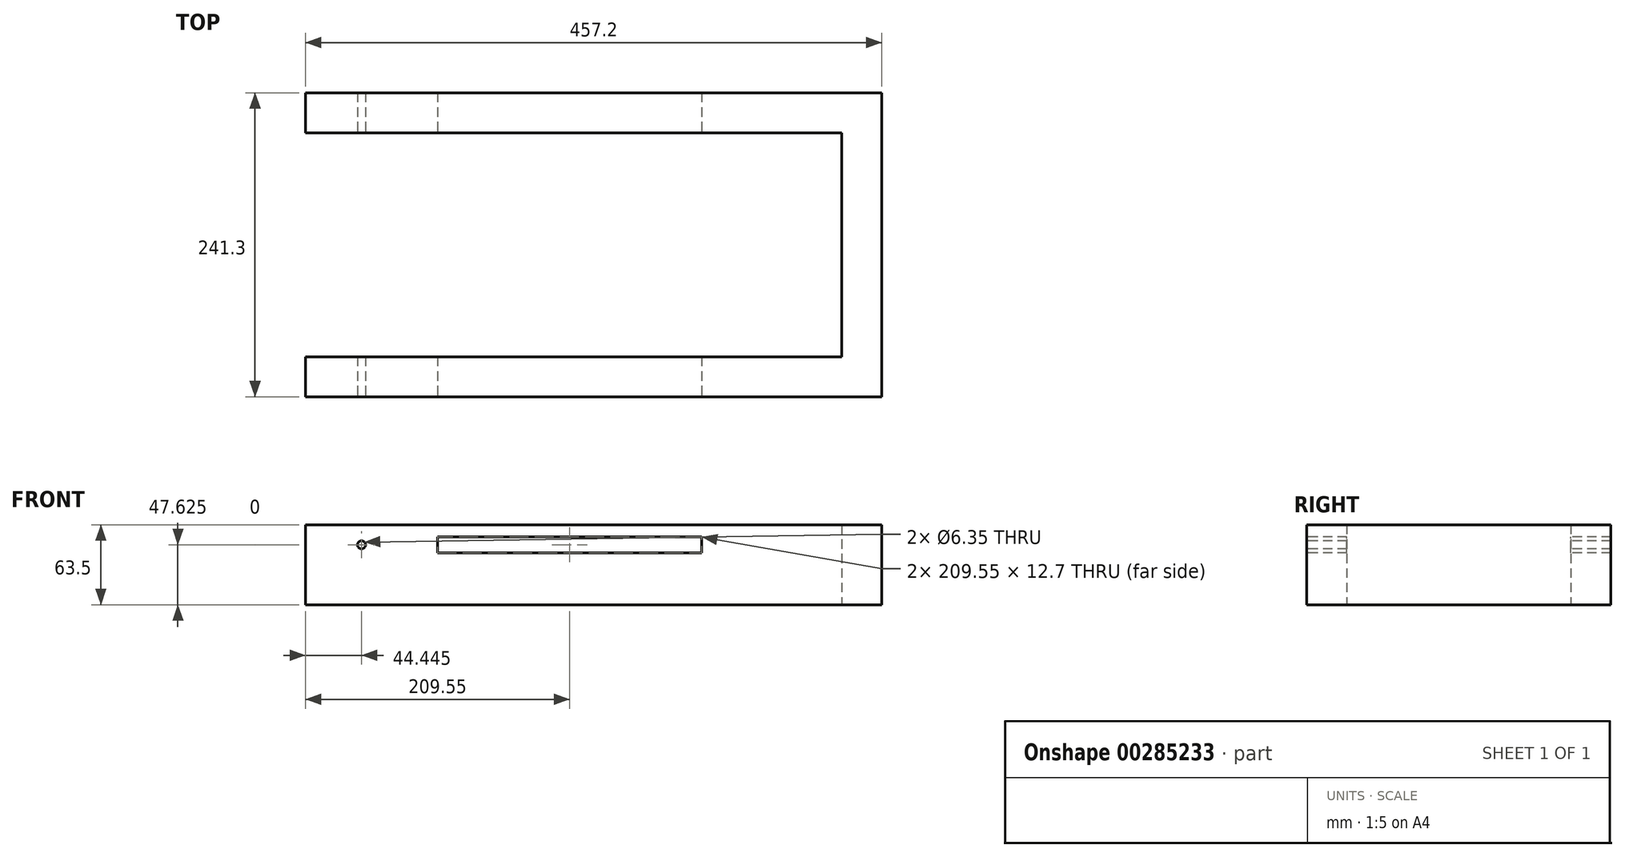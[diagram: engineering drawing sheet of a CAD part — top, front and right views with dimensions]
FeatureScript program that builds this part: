
annotation { "Feature Type Name" : "Feature", "Feature Type Description" : "" }
export const myFeature = defineFeature(function(context is Context, id is Id, definition is map)
    precondition{}
    {
        {
            var Q0;
            Q0=qCreatedBy(makeId("Front.planeOp"),FACE);
            var sketch = newSketch(context, id + "F0", { "sketchPlane" : qUnion([Q0])});
            skLineSegment(sketch, "E0.bottom", {"start": v(0, 0) * mm, "end": v(457.2, 0) * mm});
            skLineSegment(sketch, "E0.top", {"start": v(0, 63.5) * mm, "end": v(457.2, 63.5) * mm});
            skLineSegment(sketch, "E0.left", {"start": v(0, 0) * mm, "end": v(0, 63.5) * mm});
            skLineSegment(sketch, "E0.right", {"start": v(457.2, 0) * mm, "end": v(457.2, 63.5) * mm});
            skSolve(sketch);
        }
        {
            var Q0;
            Q0=makeQuery(id+"F0.imprint","IMPRINT",FACE,{"disambiguationData":[TD([[makeQuery(id+"F0.imprint","IMPRINT",EDGE,{"derivedFrom":sQuery(id+"F0.wireOp",EDGE,"E0.bottom")}),1.0]])]});
            extrude(context, id + "F1", {"entities" : qUnion([Q0]), "depth" : 31.75 * mm});
        }
        {
            var Q0;
            Q0=makeQuery(id+"F1.opExtrude","CAP_FACE",FACE,{"disambiguationData":[OSD([sQuery(id+"F0.wireOp",EDGE,"E0.bottom"),sQuery(id+"F0.wireOp",EDGE,"E0.top"),sQuery(id+"F0.wireOp",EDGE,"E0.left"),sQuery(id+"F0.wireOp",EDGE,"E0.right")])],"isStart":false});
            var sketch = newSketch(context, id + "F2", { "sketchPlane" : qUnion([Q0])});
            skLineSegment(sketch, "E1.bottom", {"start": v(457.2, 63.5) * mm, "end": v(425.45, 63.5) * mm});
            skLineSegment(sketch, "E1.top", {"start": v(457.2, 0) * mm, "end": v(425.45, 0) * mm});
            skLineSegment(sketch, "E1.left", {"start": v(457.2, 63.5) * mm, "end": v(457.2, 0) * mm});
            skLineSegment(sketch, "E1.right", {"start": v(425.45, 63.5) * mm, "end": v(425.45, 0) * mm});
            skSolve(sketch);
        }
        {
            var Q0;
            Q0=makeQuery(id+"F2.imprint","IMPRINT",FACE,{"disambiguationData":[TD([[makeQuery(id+"F2.imprint","IMPRINT",EDGE,{"derivedFrom":sQuery(id+"F2.wireOp",EDGE,"E1.bottom")}),-1.0]])]});
            extrude(context, id + "F3", {"entities" : qUnion([Q0]), "operationType" : NewBodyOperationType.ADD, "depth" : 177.8 * mm});
        }
        {
            var Q0;
            Q0=makeQuery(id+"F3.opExtrude","CAP_FACE",FACE,{"disambiguationData":[OSD([sQuery(id+"F2.wireOp",EDGE,"E1.bottom"),sQuery(id+"F2.wireOp",EDGE,"E1.top"),sQuery(id+"F2.wireOp",EDGE,"E1.left"),sQuery(id+"F2.wireOp",EDGE,"E1.right")])],"isStart":false});
            var sketch = newSketch(context, id + "F4", { "sketchPlane" : qUnion([Q0])});
            skLineSegment(sketch, "E2.bottom", {"start": v(457.2, 0) * mm, "end": v(0, 0) * mm});
            skLineSegment(sketch, "E2.top", {"start": v(457.2, 63.5) * mm, "end": v(0, 63.5) * mm});
            skLineSegment(sketch, "E2.left", {"start": v(457.2, 0) * mm, "end": v(457.2, 63.5) * mm});
            skLineSegment(sketch, "E2.right", {"start": v(0, 0) * mm, "end": v(0, 63.5) * mm});
            skSolve(sketch);
        }
        {
            var Q0;
            {var subQ0=sQuery(id+"F4.wireOp",EDGE,"E2.left");Q0=makeQuery(id+"F4.imprint","IMPRINT",FACE,{"disambiguationData":[TD([[makeQuery(id+"F4.imprint","IMPRINT",EDGE,{"derivedFrom":subQ0}),1.0]])]});}
            var Q1;
            {var subQ2=sQuery(id+"F4.wireOp",EDGE,"E2.right");Q1=makeQuery(id+"F4.imprint","IMPRINT",FACE,{"disambiguationData":[TD([[makeQuery(id+"F4.imprint","IMPRINT",EDGE,{"derivedFrom":subQ2}),-1.0]])]});}
            extrude(context, id + "F5", {"entities" : qUnion([Q0, Q1]), "operationType" : NewBodyOperationType.ADD, "depth" : 31.75 * mm});
        }
        {
            var Q0;
            Q0=makeQuery(id+"FYPlNWS78pAfCIl_1.boolean.opBoolean","MERGE",FACE,{"derivedFrom":[makeQuery(id+"F5.opExtrude","CAP_FACE",FACE,{"disambiguationData":[OSD([sQuery(id+"F4.wireOp",EDGE,"E2.bottom"),sQuery(id+"F4.wireOp",EDGE,"E2.top"),sQuery(id+"F4.wireOp",EDGE,"E2.left"),sQuery(id+"F4.wireOp",EDGE,"E2.right")])],"isStart":false}),makeQuery(id+"FYPlNWS78pAfCIl_1.opExtrude","SWEPT_FACE",FACE,{"disambiguationData":[OSD([sQuery(id+"FyuM1HVr1UCOXRJ_1.wireOp",EDGE,"lGIyAuJV-Nt9h-qGPY-NSEo-xbKzYlnuy3f9.bottom")])]})]});
            var sketch = newSketch(context, id + "F6", { "sketchPlane" : qUnion([Q0])});
            skLineSegment(sketch, "E3", {"start": v(457.2, 63.5) * mm, "end": v(393.7, 63.5) * mm});
            skLineSegment(sketch, "E4", {"start": v(393.7, 63.5) * mm, "end": v(101.6, 63.5) * mm});
            skLineSegment(sketch, "E5", {"start": v(101.6, 63.5) * mm, "end": v(247.65, 63.5) * mm});
            skLineSegment(sketch, "E6", {"start": v(247.65, 63.5) * mm, "end": v(247.65, 47.62) * mm});
            skLineSegment(sketch, "E7.bottom", {"start": v(314.33, 41.28) * mm, "end": v(180.98, 41.28) * mm});
            skLineSegment(sketch, "E7.top", {"start": v(314.33, 53.97) * mm, "end": v(180.98, 53.97) * mm});
            skLineSegment(sketch, "E7.left", {"start": v(314.33, 41.28) * mm, "end": v(314.33, 53.98) * mm});
            skLineSegment(sketch, "E7.right", {"start": v(180.98, 41.28) * mm, "end": v(180.98, 53.98) * mm});
            skPoint(sketch, "E7.middle", {"position": v(247.65, 47.62) * mm});
            skSolve(sketch);
        }
        {
            var Q0;
            Q0=makeQuery(id+"F6.imprint","IMPRINT",FACE,{"disambiguationData":[TD([[makeQuery(id+"F6.imprint","IMPRINT",EDGE,{"derivedFrom":sQuery(id+"F6.wireOp",EDGE,"E7.bottom")}),-1.0]])]});
            extrude(context, id + "F7", {"entities" : qUnion([Q0]), "operationType" : NewBodyOperationType.REMOVE, "oppositeDirection" : true, "depth" : 254 * mm});
        }
        {
            var Q0;
            Q0=makeQuery(id+"FYPlNWS78pAfCIl_1.boolean.opBoolean","MERGE",FACE,{"derivedFrom":[makeQuery(id+"F5.opExtrude","CAP_FACE",FACE,{"disambiguationData":[OSD([sQuery(id+"F4.wireOp",EDGE,"E2.bottom"),sQuery(id+"F4.wireOp",EDGE,"E2.top"),sQuery(id+"F4.wireOp",EDGE,"E2.left"),sQuery(id+"F4.wireOp",EDGE,"E2.right")])],"isStart":false}),makeQuery(id+"FYPlNWS78pAfCIl_1.opExtrude","SWEPT_FACE",FACE,{"disambiguationData":[OSD([sQuery(id+"FyuM1HVr1UCOXRJ_1.wireOp",EDGE,"lGIyAuJV-Nt9h-qGPY-NSEo-xbKzYlnuy3f9.bottom")])]})]});
            var sketch = newSketch(context, id + "F8", { "sketchPlane" : qUnion([Q0])});
            skLineSegment(sketch, "E8", {"start": v(31.74, 63.5) * mm, "end": v(31.74, 47.62) * mm});
            skLineSegment(sketch, "E9", {"start": v(31.74, 47.62) * mm, "end": v(44.44, 47.62) * mm});
            skCircle(sketch, "E10", {"center": v(44.44, 47.62) * mm, "radius": 3.18 * mm});
            skSolve(sketch);
        }
        {
            var Q0;
            Q0=makeQuery(id+"F8.imprint","IMPRINT",FACE,{"disambiguationData":[TD([[makeQuery(id+"F8.imprint","IMPRINT",EDGE,{"derivedFrom":sQuery(id+"F8.wireOp",EDGE,"E10")}),1.0]])]});
            extrude(context, id + "F9", {"entities" : qUnion([Q0]), "operationType" : NewBodyOperationType.REMOVE, "oppositeDirection" : true, "depth" : 508 * mm});
        }
        {
            var Q0;
            Q0=makeQuery(id+"FYPlNWS78pAfCIl_1.boolean.opBoolean","MERGE",FACE,{"derivedFrom":[makeQuery(id+"F5.opExtrude","CAP_FACE",FACE,{"disambiguationData":[OSD([sQuery(id+"F4.wireOp",EDGE,"E2.bottom"),sQuery(id+"F4.wireOp",EDGE,"E2.top"),sQuery(id+"F4.wireOp",EDGE,"E2.left"),sQuery(id+"F4.wireOp",EDGE,"E2.right")])],"isStart":false}),makeQuery(id+"FYPlNWS78pAfCIl_1.opExtrude","SWEPT_FACE",FACE,{"disambiguationData":[OSD([sQuery(id+"FyuM1HVr1UCOXRJ_1.wireOp",EDGE,"lGIyAuJV-Nt9h-qGPY-NSEo-xbKzYlnuy3f9.bottom")])]})]});
            var sketch = newSketch(context, id + "F10", { "sketchPlane" : qUnion([Q0])});
            skLineSegment(sketch, "E11.bottom", {"start": v(180.98, 41.28) * mm, "end": v(104.78, 41.28) * mm});
            skLineSegment(sketch, "E11.top", {"start": v(180.98, 53.98) * mm, "end": v(104.78, 53.98) * mm});
            skLineSegment(sketch, "E11.left", {"start": v(180.98, 41.28) * mm, "end": v(180.98, 53.98) * mm});
            skLineSegment(sketch, "E11.right", {"start": v(104.78, 41.27) * mm, "end": v(104.78, 53.98) * mm});
            skSolve(sketch);
        }
        {
            var Q0;
            Q0=makeQuery(id+"F10.imprint","IMPRINT",FACE,{"disambiguationData":[TD([[makeQuery(id+"F10.imprint","IMPRINT",EDGE,{"derivedFrom":sQuery(id+"F10.wireOp",EDGE,"E11.bottom")}),-1.0]])]});
            extrude(context, id + "F11", {"entities" : qUnion([Q0]), "operationType" : NewBodyOperationType.REMOVE, "oppositeDirection" : true, "depth" : 346.7 * mm});
        }
    });
